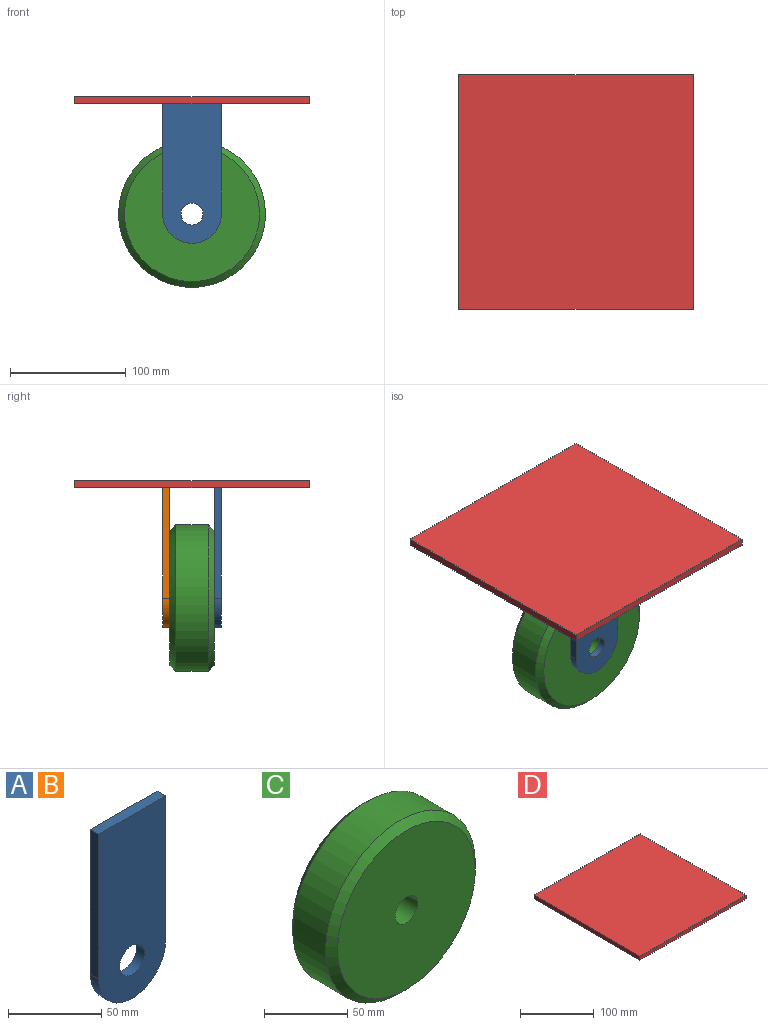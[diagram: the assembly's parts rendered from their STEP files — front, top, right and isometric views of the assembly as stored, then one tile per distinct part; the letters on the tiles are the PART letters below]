
ASSEMBLY  parts=4 mates=3
PART A: 7 faces, bbox 50.8x6.4x120.7 mm
  f0: plane 95.25x6.35mm, normal (1,0,0), area 604.8mm2, adj f1,f3,f5,f6
  f1: plane 50.8x6.35mm, normal (0,0,1), area 322.6mm2, adj f0,f2,f5,f6
  f2: plane 95.25x6.35mm, normal (-1,0,0), area 604.8mm2, adj f1,f3,f5,f6
  f3: cylinder r=25.4mm len=50.8mm, axis (0,1,0), area 506.7mm2, adj f0,f2,f5,f6
  f4: cylinder r=9.53mm len=19.05mm, axis (0,1,0), area 380mm2, adj f5,f6
  f5: plane 120.65x50.8mm, normal (0,-1,0), area 5567.1mm2, adj f0,f1,f2,f3,f4
  f6: plane 120.65x50.8mm, normal (0,1,0), area 5567.1mm2, adj f0,f1,f2,f3,f4
PART B: same geometry as A
PART C: 6 faces, bbox 127x38.1x127 mm
  f0: cylinder r=9.53mm len=38.1mm, axis (0,1,0), area 2280.2mm2, adj f2,f3
  f1: cylinder r=63.5mm len=127mm, axis (0,1,0), area 11147.6mm2, adj f4,f5
  f2: plane 116.84x116.84mm, normal (0,-1,0), area 10436.9mm2, adj f0,f5
  f3: plane 116.84x116.84mm, normal (0,1,0), area 10436.9mm2, adj f0,f4
  f4: cone r=63.5mm half-angle=45deg, axis (0,-1,0), area 2751.7mm2, adj f1,f3
  f5: cone r=58.42mm half-angle=45deg, axis (0,1,0), area 2751.7mm2, adj f1,f2
PART D: 6 faces, bbox 203.2x203.2x6.4 mm
  f0: plane 203.2x6.35mm, normal (1,0,0), area 1290.3mm2, adj f1,f3,f4,f5
  f1: plane 203.2x6.35mm, normal (0,1,0), area 1290.3mm2, adj f0,f2,f4,f5
  f2: plane 203.2x6.35mm, normal (-1,0,0), area 1290.3mm2, adj f1,f3,f4,f5
  f3: plane 203.2x6.35mm, normal (0,-1,0), area 1290.3mm2, adj f0,f2,f4,f5
  f4: plane 203.2x203.2mm, normal (0,0,1), area 41290.2mm2, adj f0,f1,f2,f3
  f5: plane 203.2x203.2mm, normal (0,0,-1), area 41290.2mm2, adj f0,f1,f2,f3
PLACE A t=(-118.71,-26.83,-7.29)mm
PLACE B t=(-118.71,17.62,-7.29)mm
PLACE C t=(-118.71,11.27,-7.29)mm
PLACE D t=(-118.71,-7.78,87.96)mm
MATE fastened B.f1 <-> D.f5  axis (0,0,1) through (-118.71,14.45,87.96)mm
MATE cylindrical C.f0 <-> A.f4  axis (0,-1,0) through (-118.71,-26.83,-7.29)mm
MATE fastened A.f1 <-> D.f5  axis (0,0,1) through (-118.71,-30,87.96)mm
